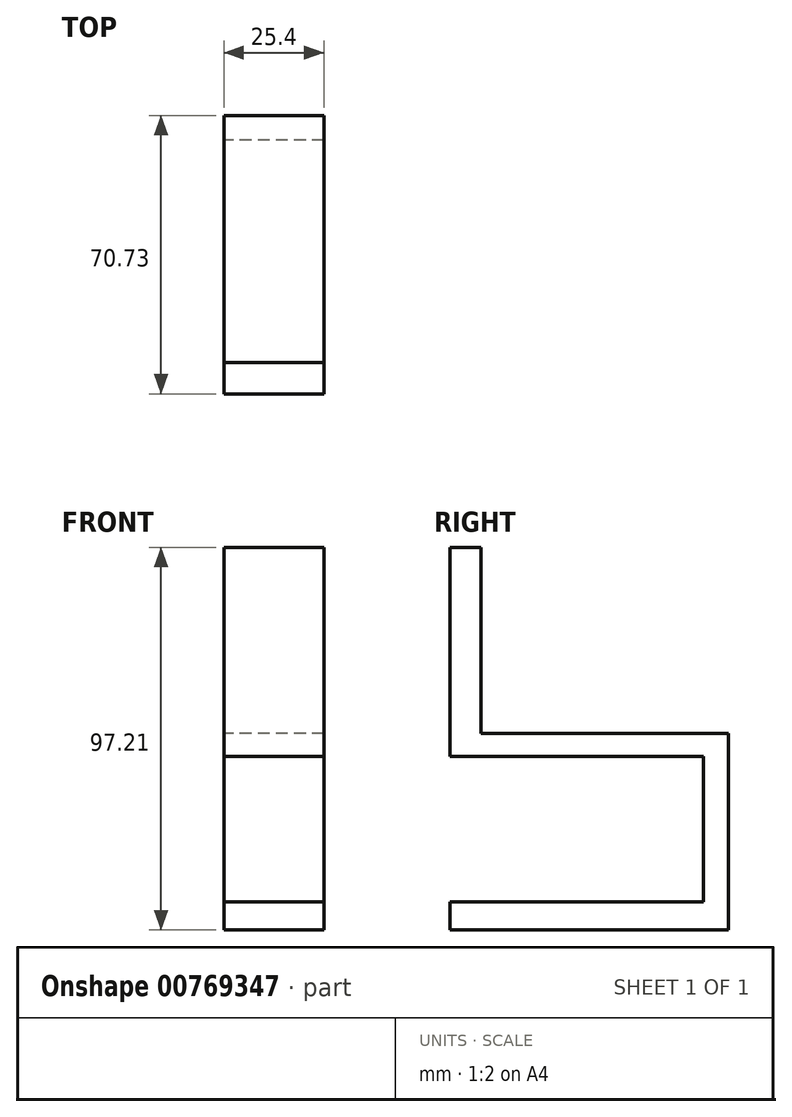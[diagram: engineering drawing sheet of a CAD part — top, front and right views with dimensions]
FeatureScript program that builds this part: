
annotation { "Feature Type Name" : "Feature", "Feature Type Description" : "" }
export const myFeature = defineFeature(function(context is Context, id is Id, definition is map)
    precondition{}
    {
        {
            var Q0;
            Q0=qCreatedBy(makeId("Right.planeOp"),FACE);
            var sketch = newSketch(context, id + "F0", { "sketchPlane" : qUnion([Q0])});
            skLineSegment(sketch, "E0", {"start": v(-45.74, 0) * mm, "end": v(-45.74, 53.11) * mm});
            skLineSegment(sketch, "E1", {"start": v(-45.74, 53.11) * mm, "end": v(-37.82, 53.11) * mm});
            skLineSegment(sketch, "E2", {"start": v(-37.82, 53.11) * mm, "end": v(-37.82, 5.87) * mm});
            skLineSegment(sketch, "E3", {"start": v(-37.82, 5.87) * mm, "end": v(24.99, 5.87) * mm});
            skLineSegment(sketch, "E4", {"start": v(24.99, 5.87) * mm, "end": v(24.99, -44.1) * mm});
            skLineSegment(sketch, "E5", {"start": v(24.99, -44.1) * mm, "end": v(-45.74, -44.1) * mm});
            skLineSegment(sketch, "E6", {"start": v(-45.74, -44.1) * mm, "end": v(-45.74, -37) * mm});
            skLineSegment(sketch, "E7", {"start": v(-45.74, -37) * mm, "end": v(18.7, -37) * mm});
            skLineSegment(sketch, "E8", {"start": v(18.7, -37) * mm, "end": v(18.7, 0) * mm});
            skLineSegment(sketch, "E9", {"start": v(18.7, 0) * mm, "end": v(-45.74, 0) * mm});
            skSolve(sketch);
        }
        {
            var Q0;
            Q0 = qSketchRegion(id + "F0", true);
            extrude(context, id + "F1", {"entities" : qUnion([Q0]), "depth" : 25.4 * mm, "offsetDistance" : 25.4 * mm});
        }
    });
